# Revit family: X-Connection-Bracket-Steel & Tube-Speed Channel
name_source: partatom
category: Structural Connections
revit_build: Autodesk Revit 2017 (Build: 20170118_1100(x64)
units: mm (PartAtom-declared; Revit-internal decimal feet)

## family parameters
Cut with Voids When Loaded = No
Enable cutting in views = Yes
Host = Face
Material for Model Behavior = Steel
OmniClass Number = 23.25.05.17.11
OmniClass Title = Column Bases
Shared = Yes

## types (1)
- Standard
    Assembly Code = B1020230
    CBICode = 3411
    CBIDescription = Structural steelwork
    Default Elevation = 0 mm  [stored 0 ft]
    Description = HST Steel Purlins and Girts are high strength lipped profile sections, providing an economic solution for your building project.
    Design Instruction = All the design information should be cross referenced with the current Steel & Tube Purlins and Girts design guide, and AS/NZS 4600:2005
    Design Standard = Steel & Tube’s HST purlins and Girts profiles are designed in accordance with AS/NZS 4600:2005.
    Manufacturer = Steel & Tube
    ManufacturerName = Steel & Tube
    ManufacturerURL = http://www.steelandtube.co.nz
    Material Standard = Steel & Tube’s HST purlins and Girts profiles are manufactured from materials conforming to AS1397:2011
    ModifiedIssue_ANZRS = 20160602 $
    PlateThickness_ANZRS = 1 mm  [stored 0.00328084 ft]
    SpecificationDescription = Steel & Tube Purlins & Girts
    SpecificationReference = 3411ST
    Type Comments = HST Steel Purlin Standard Cleat
    URL = http://www.steelandtube.co.nz
    Uniclass2015Code = Pr_20_76_51_21
    Uniclass2015Title = Cold-formed galvanized steel sections
    Uniclass2015Version = 2015

note: [stored X ft] marks values corroborated as IEEE doubles in the binary element streams (Revit-internal decimal feet)

## geometry (parser evidence)
native form markers: Sweep x2
no freeform markers — native parametric forms only
